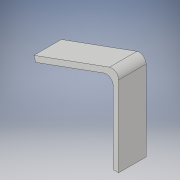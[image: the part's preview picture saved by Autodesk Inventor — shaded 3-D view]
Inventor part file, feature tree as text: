
AUTODESK INVENTOR PART (.ipt)
format: ipt  version: 2017 (Build 210142000, 142)  size: 103,424 bytes
history: native  units: in
note: dims shown in document units (in); Inventor stores cm internally (conversion verified against a paired STEP export)
features: extrude x1, fillet x1, sketch x1
ambient origin geometry x8: Origin, YZ Plane, XZ Plane, XY Plane, X Axis, Y Axis, Z Axis, Center Point
bodies: Solid1 (feature_tree)
feature tree (3):
  extrude  "Extrusion1"  Depth=1.5in
  fillet  "Fillet1"  Radius=0.481in
  sketch  "Sketch1"  dims[d0=1.5in d1=1.5in d2=0.481in d3=0.1in d4=0.1in d5=0.5in d6=0.0in d7=0.125in]
